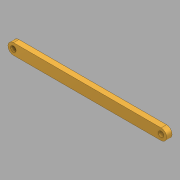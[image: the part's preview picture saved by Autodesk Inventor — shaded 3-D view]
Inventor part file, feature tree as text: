
AUTODESK INVENTOR PART (.ipt)
format: ipt  version: 2020 (Build 240168000, 168)  size: 90,112 bytes
history: native  units: in
note: dims shown in document units (in); Inventor stores cm internally (conversion verified against a paired STEP export)
features: other x1, extrude x1, sketch x1
ambient origin geometry x8: Origin, YZ Plane, XZ Plane, XY Plane, X Axis, Y Axis, Z Axis, Center Point
bodies: Body1 (feature_tree)
feature tree (3):
  other  "Sólido1"
  extrude  "Extrusión1"  Depth=0.125in
  sketch  "Boceto1"  dims[d0=1.6875in d5=0.125in d6=0.125in d7=0.0625in d8=0.0625in d9=0.0625in d10=0.0in]
